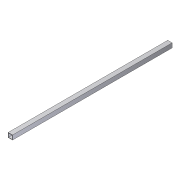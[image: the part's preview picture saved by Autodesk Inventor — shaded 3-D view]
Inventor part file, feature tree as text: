
AUTODESK INVENTOR PART (.ipt)
format: ipt  version: 2012 (Build 160160000, 160)  size: 70,656 bytes
history: native  units: in
note: dims shown in document units (in); Inventor stores cm internally (conversion verified against a paired STEP export)
features: extrude x1, sketch x1
ambient origin geometry x8: Origin, YZ Plane, XZ Plane, XY Plane, X Axis, Y Axis, Z Axis, Center Point
bodies: Solid1 (feature_tree)
feature tree (2):
  extrude  "Extrusion1"  Depth=1.25in
  sketch  "Sketch1"  dims[d0=0.125in d1=1.25in d2=45.5in d3=0.0in]
